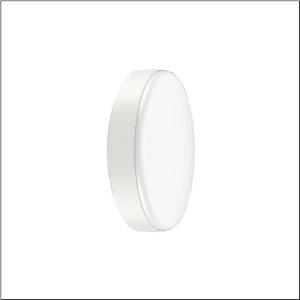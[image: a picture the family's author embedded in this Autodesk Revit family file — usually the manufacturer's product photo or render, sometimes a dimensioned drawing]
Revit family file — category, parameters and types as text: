
# Revit family: rondel_31_51wc10mb34as
name_source: partatom
category: Lighting Fixtures
units: mm (PartAtom-declared; Revit-internal decimal feet)

## family parameters
Cut with Voids When Loaded = No
Host = Face
Light Source = No
Part Type = Normal
Room Calculation Point = No
Round Connector Dimension = Use Diameter
Shared = No

## types (1)
- --- (1 x LED, 4250 lm, 35.4 W, 3000K)
    Apparent Load = 35 VA
    CIE Flux Codes = 44 75 94 94 100
    Color Rendering = 80
    Color Temperature = 3000K
    Default Elevation = 1800 mm
    Description = Rondel 31, wall and ceiling luminaire, primary optical cover: cover, of PC, opal, light emission: direct distribution, primary light characteristic: symmetric, installation type: surface-mounted, LED, rated luminous flux: 4.250lm, luminous efficacy: 120lm/W, light colour: 830, colour temperature: 3000K, with terminal, 3-pole, max. 2.5mm², mains connection: 220..240V, AC, 50/60Hz, rated input power: 35W, luminaire housing, of PC, traffic white (RAL 9016), diameter: 480mm, brightness and presence sensor, HF sensor, protection rating (complete): IP65, insulation class (complete): insulation class II (safety insulation), certification: CE, impact resistance: IK10, permissible operating ambient temperature: -20..+40°C, permissible storage temperature: -20..+60°C, packaging unit: 1 piece
    Height = 97 mm
    Lamp = 1 x LED
    Lamp Light Flux = 4250 lm
    Lamp Power = 35.4 W
    Lamp count = 1
    Length = 480 mm
    Luminous efficacy = 120 lm/W
    Manufacturer = Siteco
    ModVariant = No
    Model = 51WC10MB34AS
    Mounting Place = Ceiling
    Mounting Type = Surface mounted
    Number of Poles = 1
    OnlyDefault = Yes
    Power Factor = 1
    Product Name = Rondel 31
    Product group = wall and ceiling luminaire
    ProductGroupID = 301
    Protection Class = Protection class II
    Protection Degree = IP 65
    RLX_Detail_Level = 1
    RLX_Emergency_Light_Flux = 0 lm
    RLX_Emergency_Type = 0
    RLX_Emergency_Type_DB = No
    RlxData = <blob elided: 41421 chars, md5=61eadc04>
    Socket = socket
    Standby Power = 0 W
    System Light Flux = 4250 lm
    System Power = 35 W
    Type Comments = factory setting: luminous flux: 100 % | (ON | ON)
    Type Image = l_1007188.jpg
    URL = http://relux.com
    VarID = @adj_041933
    Voltage = 0 V
    Weight = 0.00 kg
    Width = 0 mm  [stored 0 ft]

note: [stored X ft] marks values corroborated as IEEE doubles in the binary element streams (Revit-internal decimal feet)

## geometry (parser evidence)
native form markers: Blend x4, Sweep x12
no freeform markers — native parametric forms only
